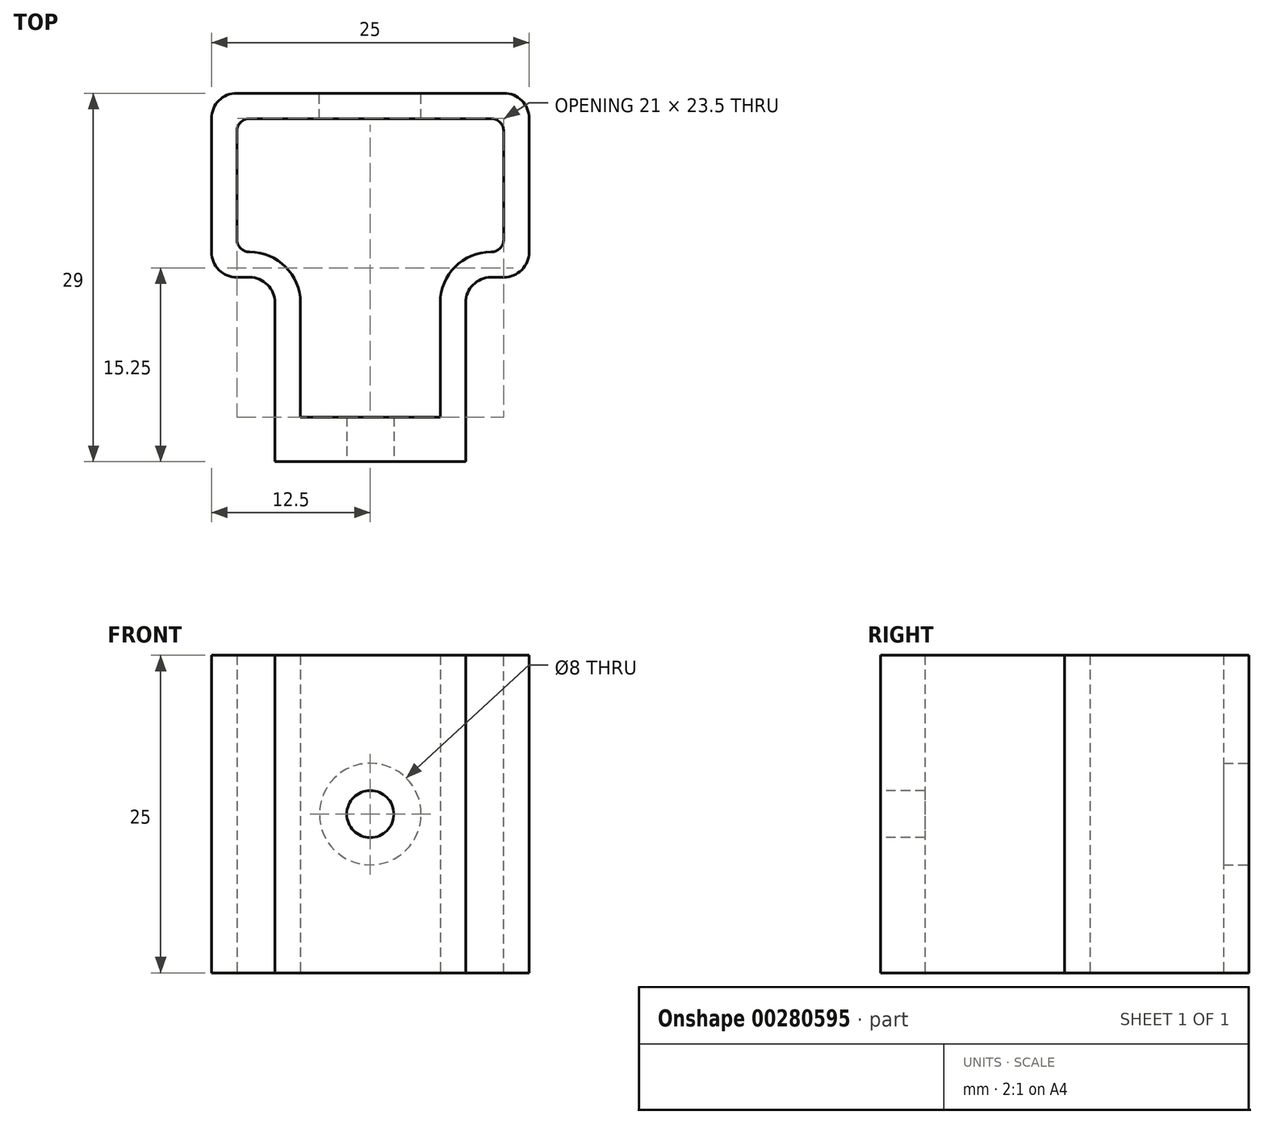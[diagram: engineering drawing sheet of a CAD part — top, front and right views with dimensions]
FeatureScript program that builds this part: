
annotation { "Feature Type Name" : "Feature", "Feature Type Description" : "" }
export const myFeature = defineFeature(function(context is Context, id is Id, definition is map)
    precondition{}
    {
        {
            var Q0;
            Q0=qCreatedBy(makeId("Top.planeOp"),FACE);
            var sketch = newSketch(context, id + "F0", { "sketchPlane" : qUnion([Q0])});
            skLineSegment(sketch, "E0", {"start": v(-7.5, -14.5) * mm, "end": v(7.5, -14.5) * mm});
            skLineSegment(sketch, "E1", {"start": v(-10.5, 14.5) * mm, "end": v(10.5, 14.5) * mm});
            skLineSegment(sketch, "E2", {"start": v(-12.5, 12.5) * mm, "end": v(-12.5, 2) * mm});
            skLineSegment(sketch, "E3", {"start": v(-7.5, -14.5) * mm, "end": v(-7.5, -2) * mm});
            skLineSegment(sketch, "E4", {"start": v(-9.5, 0) * mm, "end": v(-10.5, 0) * mm});
            skLineSegment(sketch, "E5", {"start": v(7.5, -14.5) * mm, "end": v(7.5, -2) * mm});
            skLineSegment(sketch, "E6", {"start": v(12.5, 12.5) * mm, "end": v(12.5, 2) * mm});
            skLineSegment(sketch, "E7", {"start": v(10.5, 0) * mm, "end": v(9.5, 0) * mm});
            skPoint(sketch, "E8.visualSharp", {"position": v(-12.5, 0) * mm});
            skArc(sketch, "E8.filletArc", {"start": v(-12.5, 2) * mm, "mid": v(-11.91, 0.59) * mm, "end": v(-10.5, 0) * mm});
            skPoint(sketch, "E9.visualSharp", {"position": v(-7.5, 0) * mm});
            skArc(sketch, "E9.filletArc", {"start": v(-7.5, -2) * mm, "mid": v(-8.09, -0.59) * mm, "end": v(-9.5, 0) * mm});
            skPoint(sketch, "E10.visualSharp", {"position": v(7.5, 0) * mm});
            skArc(sketch, "E10.filletArc", {"start": v(9.5, 0) * mm, "mid": v(8.09, -0.59) * mm, "end": v(7.5, -2) * mm});
            skPoint(sketch, "E11.visualSharp", {"position": v(12.5, 0) * mm});
            skArc(sketch, "E11.filletArc", {"start": v(10.5, 0) * mm, "mid": v(11.91, 0.59) * mm, "end": v(12.5, 2) * mm});
            skPoint(sketch, "E12.visualSharp", {"position": v(12.5, 14.5) * mm});
            skArc(sketch, "E12.filletArc", {"start": v(12.5, 12.5) * mm, "mid": v(11.91, 13.91) * mm, "end": v(10.5, 14.5) * mm});
            skPoint(sketch, "E13.visualSharp", {"position": v(-12.5, 14.5) * mm});
            skArc(sketch, "E13.filletArc", {"start": v(-10.5, 14.5) * mm, "mid": v(-11.91, 13.91) * mm, "end": v(-12.5, 12.5) * mm});
            skLineSegment(sketch, "E14.0", {"start": v(-10.5, 12.5) * mm, "end": v(-10.5, 1.87) * mm});
            skArc(sketch, "E14.1", {"start": v(-5.5, -2) * mm, "mid": v(-7.05, 1.16) * mm, "end": v(-10.5, 1.87) * mm});
            skLineSegment(sketch, "E14.2", {"start": v(-10.5, 12.5) * mm, "end": v(10.5, 12.5) * mm});
            skLineSegment(sketch, "E14.3", {"start": v(-5.5, -12.5) * mm, "end": v(-5.5, -2) * mm});
            skLineSegment(sketch, "E14.4", {"start": v(10.5, 12.5) * mm, "end": v(10.5, 1.87) * mm});
            skArc(sketch, "E14.5", {"start": v(10.5, 1.87) * mm, "mid": v(7.05, 1.16) * mm, "end": v(5.5, -2) * mm});
            skLineSegment(sketch, "E14.6", {"start": v(5.5, -12.5) * mm, "end": v(5.5, -2) * mm});
            skLineSegment(sketch, "E14.7", {"start": v(-5.5, -12.5) * mm, "end": v(5.5, -12.5) * mm});
            skSolve(sketch);
        }
        {
            var Q0;
            Q0=makeQuery(id+"F0.imprint","IMPRINT",FACE,{"disambiguationData":[TD([[makeQuery(id+"F0.imprint","IMPRINT",EDGE,{"derivedFrom":sQuery(id+"F0.wireOp",EDGE,"E0")}),1.0]])]});
            extrude(context, id + "F1", {"entities" : qUnion([Q0]), "depth" : 25 * mm});
        }
        {
            var Q0;
            Q0=makeQuery(id+"F1.opExtrude","SWEPT_FACE",FACE,{"disambiguationData":[OSD([sQuery(id+"F0.wireOp",EDGE,"E0")])]});
            var sketch = newSketch(context, id + "F2", { "sketchPlane" : qUnion([Q0])});
            skLineSegment(sketch, "E15", {"start": v(-7.5, 25) * mm, "end": v(7.5, 0) * mm, "construction": true});
            skLineSegment(sketch, "E16", {"start": v(-7.5, 0) * mm, "end": v(7.5, 25) * mm, "construction": true});
            skCircle(sketch, "E17", {"center": v(0, 12.5) * mm, "radius": 1.85 * mm});
            skSolve(sketch);
        }
        {
            var Q0;
            Q0=makeQuery(id+"F2.imprint","IMPRINT",FACE,{"disambiguationData":[TD([[makeQuery(id+"F2.imprint","IMPRINT",EDGE,{"derivedFrom":sQuery(id+"F2.wireOp",EDGE,"E17")}),1.0]])]});
            extrude(context, id + "F3", {"entities" : qUnion([Q0]), "operationType" : NewBodyOperationType.REMOVE, "oppositeDirection" : true, "depth" : 16.3 * mm});
        }
        {
            var Q0;
            Q0=makeQuery(id+"F1.opExtrude","SWEPT_EDGE",EDGE,{"disambiguationData":[OSD([sQuery(id+"F0.wireOp",EDGE,"E14.0"),sQuery(id+"F0.wireOp",EDGE,"E14.2")])]});
            var Q1;
            Q1=makeQuery(id+"F1.opExtrude","SWEPT_EDGE",EDGE,{"disambiguationData":[OSD([sQuery(id+"F0.wireOp",EDGE,"E14.2"),sQuery(id+"F0.wireOp",EDGE,"E14.4")])]});
            var Q2;
            Q2=makeQuery(id+"F1.opExtrude","SWEPT_EDGE",EDGE,{"disambiguationData":[OSD([sQuery(id+"F0.wireOp",EDGE,"E14.4"),sQuery(id+"F0.wireOp",EDGE,"E14.5")])]});
            var Q3;
            Q3=makeQuery(id+"F1.opExtrude","SWEPT_EDGE",EDGE,{"disambiguationData":[OSD([sQuery(id+"F0.wireOp",EDGE,"E14.0"),sQuery(id+"F0.wireOp",EDGE,"E14.1")])]});
            fillet(context, id + "F4", {"entities" : qUnion([Q0, Q1, Q2, Q3]), "radius" : 1 * mm, "tangentPropagation" : true, "allowEdgeOverflow" : false});
        }
        {
            var Q0;
            Q0=makeQuery(id+"F1.opExtrude","SWEPT_FACE",FACE,{"disambiguationData":[OSD([sQuery(id+"F0.wireOp",EDGE,"E1")])]});
            var sketch = newSketch(context, id + "F7", { "sketchPlane" : qUnion([Q0])});
            skLineSegment(sketch, "E18", {"start": v(-10.5, 25) * mm, "end": v(10.5, 0) * mm, "construction": true});
            skLineSegment(sketch, "E19", {"start": v(-10.5, 0) * mm, "end": v(10.5, 25) * mm, "construction": true});
            skCircle(sketch, "E20", {"center": v(0, 12.5) * mm, "radius": 4 * mm});
            skSolve(sketch);
        }
        {
            var Q0;
            Q0=makeQuery(id+"F7.imprint","IMPRINT",FACE,{"disambiguationData":[TD([[makeQuery(id+"F7.imprint","IMPRINT",EDGE,{"derivedFrom":sQuery(id+"F7.wireOp",EDGE,"E20")}),1.0]])]});
            extrude(context, id + "F5", {"entities" : qUnion([Q0]), "operationType" : NewBodyOperationType.REMOVE, "oppositeDirection" : true, "depth" : 8.12 * mm});
        }
        {
            var Q0;
            Q0=makeQuery(id+"F1.opExtrude","SWEPT_FACE",FACE,{"disambiguationData":[OSD([sQuery(id+"F0.wireOp",EDGE,"E14.7")])]});
            extrude(context, id + "F6", {"entities" : qUnion([Q0]), "operationType" : NewBodyOperationType.ADD, "depth" : 1.5 * mm});
        }
    });
